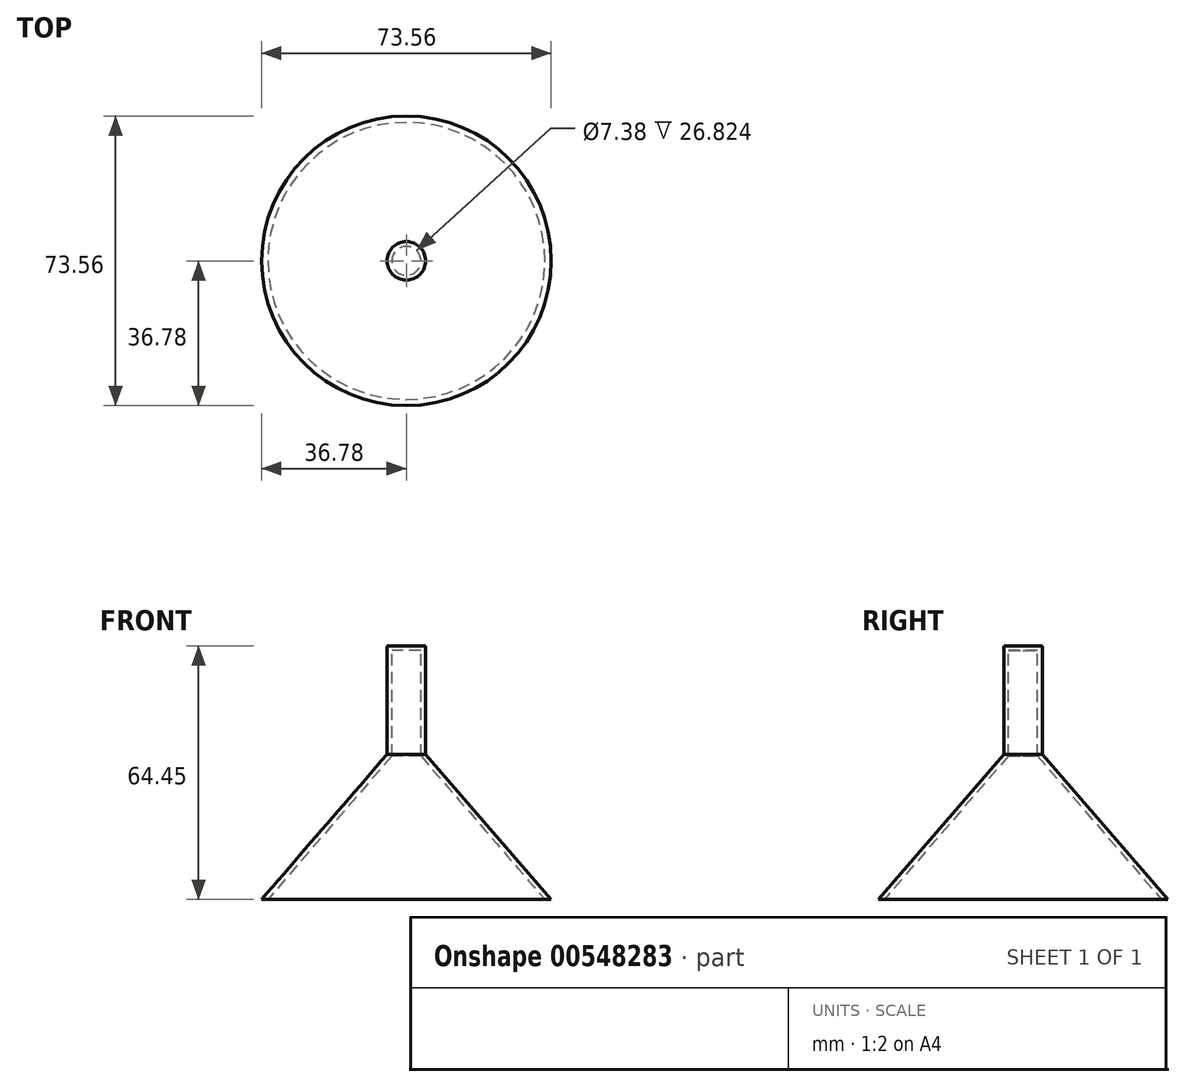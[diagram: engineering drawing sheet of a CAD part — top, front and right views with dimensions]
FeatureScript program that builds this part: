
annotation { "Feature Type Name" : "Feature", "Feature Type Description" : "" }
export const myFeature = defineFeature(function(context is Context, id is Id, definition is map)
    precondition{}
    {
        {
            var Q0;
            Q0=qCreatedBy(makeId("Front.planeOp"),FACE);
            var sketch = newSketch(context, id + "F0", { "sketchPlane" : qUnion([Q0])});
            skLineSegment(sketch, "E0", {"start": v(-35.2, 0) * mm, "end": v(-3.7, 36.42) * mm});
            skLineSegment(sketch, "E1", {"start": v(-3.7, 36.42) * mm, "end": v(-3.7, 63.25) * mm});
            skLineSegment(sketch, "E2", {"start": v(-3.7, 63.25) * mm, "end": v(0, 63.25) * mm});
            skLineSegment(sketch, "E3", {"start": v(0, 63.25) * mm, "end": v(0, 0) * mm});
            skLineSegment(sketch, "E4", {"start": v(0, 0) * mm, "end": v(-35.2, 0) * mm});
            skSolve(sketch);
        }
        {
            var Q0;
            Q0=makeQuery(id+"F0.imprint","IMPRINT",FACE,{"disambiguationData":[TD([[makeQuery(id+"F0.imprint","IMPRINT",EDGE,{"derivedFrom":sQuery(id+"F0.wireOp",EDGE,"E0")}),-1.0]])]});
            var Q1;
            Q1=sQuery(id+"F0.wireOp",EDGE,"E3");
            revolve(context, id + "F1", {"entities" : qUnion([Q0]), "axis" : qUnion([Q1]), "revolveType" : RevolveType.FULL});
        }
        {
            var Q0;
            Q0=makeQuery(id+"F1.opRevolve","SWEPT_FACE",FACE,{"disambiguationData":[OSD([sQuery(id+"F0.wireOp",EDGE,"E0")])]});
            var Q1;
            Q1=makeQuery(id+"F1.opRevolve","SWEPT_FACE",FACE,{"disambiguationData":[OSD([sQuery(id+"F0.wireOp",EDGE,"E1")])]});
            var Q2;
            Q2=makeQuery(id+"F1.opRevolve","SWEPT_FACE",FACE,{"disambiguationData":[OSD([sQuery(id+"F0.wireOp",EDGE,"E4")])]});
            var Q3;
            Q3=makeQuery(id+"F1.opRevolve","SWEPT_FACE",FACE,{"disambiguationData":[OSD([sQuery(id+"F0.wireOp",EDGE,"E2")])]});
            var Q4;
            Q4=makeQuery(id+"F1.opRevolve","SWEPT_BODY",BODY,{"disambiguationData":[OSD([sQuery(id+"F0.wireOp",EDGE,"E0"),sQuery(id+"F0.wireOp",EDGE,"E1"),sQuery(id+"F0.wireOp",EDGE,"E2"),sQuery(id+"F0.wireOp",EDGE,"E3"),sQuery(id+"F0.wireOp",EDGE,"E4")])]});
            shell(context, id + "F2", {"isHollow" : true, "entities" : qUnion([Q0, Q1, Q2, Q3]), "parts" : qUnion([Q4]), "thickness" : 1.2 * mm, "oppositeDirection" : true});
        }
        {
            var Q0;
            Q0=qCreatedBy(makeId("Top.planeOp"),FACE);
            var sketch = newSketch(context, id + "F3", { "sketchPlane" : qUnion([Q0])});
            skCircle(sketch, "E5", {"center": v(0, 0) * mm, "radius": 35.65 * mm});
            skSolve(sketch);
        }
        {
            var Q0;
            Q0=sQuery(id+"F3.wireOp",VERTEX,"E5.center");
            var Q1;
            Q1=makeQuery(id+"F1.opRevolve","SWEPT_BODY",BODY,{"disambiguationData":[OSD([sQuery(id+"F0.wireOp",EDGE,"E0"),sQuery(id+"F0.wireOp",EDGE,"E1"),sQuery(id+"F0.wireOp",EDGE,"E2"),sQuery(id+"F0.wireOp",EDGE,"E3"),sQuery(id+"F0.wireOp",EDGE,"E4")])]});
            hole(context, id + "F4", {"style" : HoleStyle.SIMPLE, "endStyle" : HoleEndStyle.THROUGH, "holeDiameter" : 300 * mm, "isTappedThrough" : true, "tappedDepth" : 12 * mm, "tapClearance" : 3, "locations" : qUnion([Q0]), "scope" : qUnion([Q1])});
        }
    });
